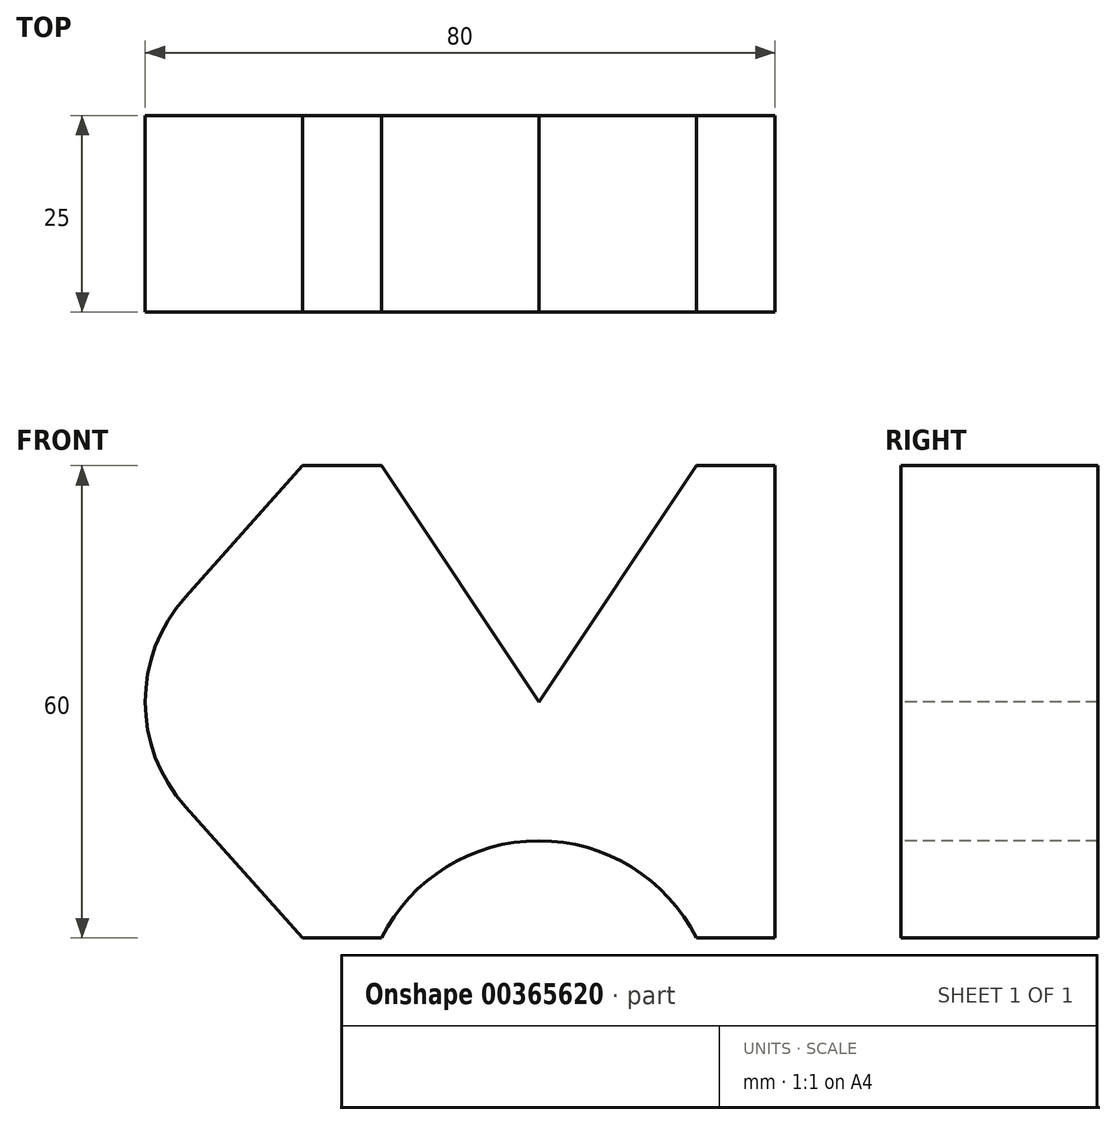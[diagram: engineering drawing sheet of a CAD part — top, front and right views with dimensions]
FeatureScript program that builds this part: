
annotation { "Feature Type Name" : "Feature", "Feature Type Description" : "" }
export const myFeature = defineFeature(function(context is Context, id is Id, definition is map)
    precondition{}
    {
        {
            var Q0;
            Q0=qCreatedBy(makeId("Front.planeOp"),FACE);
            var sketch = newSketch(context, id + "F0", { "sketchPlane" : qUnion([Q0])});
            skLineSegment(sketch, "E0", {"start": v(0, 0) * mm, "end": v(-20, 30) * mm});
            skLineSegment(sketch, "E1", {"start": v(-20, 30) * mm, "end": v(-30, 30) * mm});
            skLineSegment(sketch, "E2", {"start": v(-30, 30) * mm, "end": v(-44.9, 13.33) * mm});
            skLineSegment(sketch, "E3", {"start": v(0, 0) * mm, "end": v(20, 30) * mm});
            skLineSegment(sketch, "E4", {"start": v(20, 30) * mm, "end": v(30, 30) * mm});
            skLineSegment(sketch, "E5", {"start": v(30, 30) * mm, "end": v(30, -30) * mm});
            skLineSegment(sketch, "E6", {"start": v(30, -30) * mm, "end": v(20, -30) * mm});
            skLineSegment(sketch, "E7", {"start": v(-20, -30) * mm, "end": v(-30, -30) * mm});
            skLineSegment(sketch, "E8", {"start": v(-30, -30) * mm, "end": v(-44.9, -13.33) * mm});
            skLineSegment(sketch, "E9", {"start": v(0, 25.74) * mm, "end": v(0, -16.62) * mm, "construction": true});
            skArc(sketch, "E10", {"start": v(-44.9, 13.33) * mm, "mid": v(-50, 0) * mm, "end": v(-44.9, -13.33) * mm});
            skLineSegment(sketch, "E11", {"start": v(-30, 30) * mm, "end": v(-30, -13.33) * mm, "construction": true});
            skArc(sketch, "E12", {"start": v(-20, -30) * mm, "mid": v(0, -17.64) * mm, "end": v(20, -30) * mm});
            skSolve(sketch);
        }
        {
            var Q0;
            Q0=makeQuery(id+"F0.imprint","IMPRINT",FACE,{"disambiguationData":[TD([[makeQuery(id+"F0.imprint","IMPRINT",EDGE,{"derivedFrom":sQuery(id+"F0.wireOp",EDGE,"E0")}),1.0]])]});
            extrude(context, id + "F1", {"entities" : qUnion([Q0]), "oppositeDirection" : true, "depth" : 25 * mm});
        }
    });
